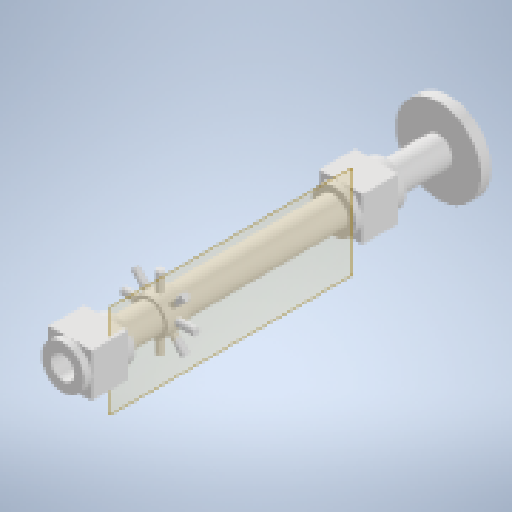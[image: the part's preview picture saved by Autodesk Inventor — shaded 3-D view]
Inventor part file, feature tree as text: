
AUTODESK INVENTOR PART (.ipt)
format: ipt  version: 2023 (Build 270158000, 158)  size: 248,832 bytes
history: native  units: mm
features: extrude x12, sketch x12, plane x1, pattern_circular x1
ambient origin geometry x8: Origin, YZ Plane, XZ Plane, XY Plane, X Axis, Y Axis, Z Axis, Center Point
bodies: Solid1 (feature_tree)
feature tree (26):
  extrude  "Extrusion1"  Depth=23.5mm
  extrude  "Extrusion2"  Depth=8.0mm
  extrude  "Extrusion3"  Depth=12.0mm
  extrude  "Extrusion4"  Depth=10.0mm TaperAngle=0.0deg
  extrude  "Extrusion5"  Depth=45.0mm TaperAngle=0.0deg
  extrude  "Extrusion6"  Depth=10.0mm TaperAngle=0.0deg
  extrude  "Extrusion7"  Depth=10.0mm TaperAngle=0.0deg
  extrude  "Extrusion8"  Depth=10.0mm TaperAngle=0.0deg
  extrude  "Extrusion9"  Depth=5.0mm TaperAngle=0.0deg
  extrude  "Extrusion10"  [1 undecoded]
  extrude  "Extrusion11"  [1 undecoded]
  plane  "Work Plane1"
  extrude  "Extrusion12"  [1 undecoded]
  pattern_circular  "Circular Pattern1"  [2 undecoded]
  sketch  "Sketch1"  dims[d0=6.5mm d1=23.5mm]
  sketch  "Sketch2"  dims[d2=3.0mm d3=0.0mm d4=8.0mm]
  sketch  "Sketch3"  dims[d5=15.0mm d6=0.0mm d7=12.0mm]
  sketch  "Sketch4"  dims[d8=2.0mm d9=0.0mm d10=10.0mm d11=0.0mm]
  sketch  "Sketch5"  dims[d12=2.0mm d13=0.0mm d14=45.0mm d15=0.0mm]
  sketch  "Sketch6"  dims[d16=10.0mm d17=6.0mm d18=0.0mm]
  sketch  "Sketch7"  dims[d19=10.0mm d20=0.0mm d21=2.0mm d22=0.0mm]
  sketch  "Sketch8"  dims[d23=10.0mm d24=0.0mm d25=2.0mm d26=0.0mm]
  sketch  "Sketch9"  dims[d27=2.0mm d28=5.0mm d29=0.5mm d30=0.0mm d31=0.0mm]
  sketch  "Sketch10"  dims[d32=80.0mm d33=360.0deg]
  sketch  "Sketch11"
  sketch  "Sketch12"
note: 5 required parameter values undecoded (feature->parameter linkage not recoverable at this tier; creation-order binding heuristic only, values carry confidence <= 0.55)
